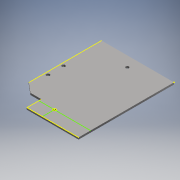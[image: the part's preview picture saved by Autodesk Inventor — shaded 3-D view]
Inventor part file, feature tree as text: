
AUTODESK INVENTOR PART (.ipt)
format: ipt  version: 2017 (Build 210142000, 142)  size: 120,320 bytes
history: native  units: in
note: dims shown in document units (in); Inventor stores cm internally (conversion verified against a paired STEP export)
features: sketch x5, other x3
ambient origin geometry x8: Origin, YZ Plane, XZ Plane, XY Plane, X Axis, Y Axis, Z Axis, Center Point
bodies: Solid1 (feature_tree)
feature tree (8):
  other  "flywheel plate.ipt"
  sketch  "Sketch4"
  sketch  "Sketch5"
  other  "Solid1::flywheel plate.ipt"
  other  "TaggingFeature1"
  sketch  "Sketch1"  dims[d0=0.3937in]
  sketch  "Sketch2"
  sketch  "Sketch3"
